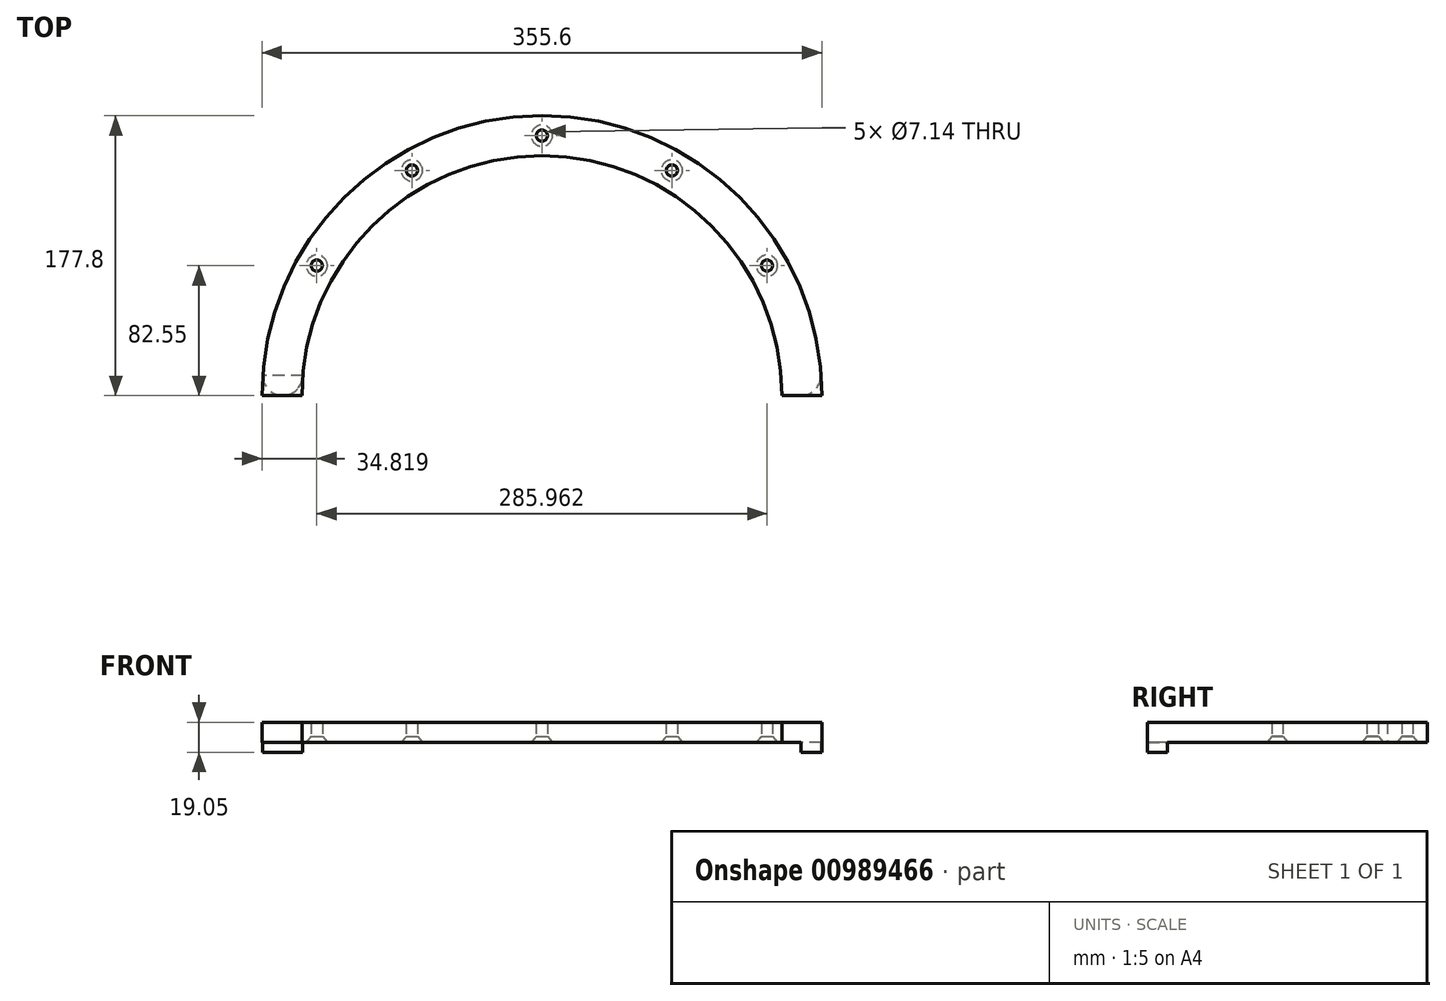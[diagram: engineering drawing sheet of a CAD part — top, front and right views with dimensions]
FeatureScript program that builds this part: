
annotation { "Feature Type Name" : "Feature", "Feature Type Description" : "" }
export const myFeature = defineFeature(function(context is Context, id is Id, definition is map)
    precondition{}
    {
        {
            var Q0;
            Q0=qCreatedBy(makeId("Top.planeOp"),FACE);
            var sketch = newSketch(context, id + "F0", { "sketchPlane" : qUnion([Q0])});
            skArc(sketch, "E0", {"start": v(-152.4, 0) * mm, "mid": v(0, 152.4) * mm, "end": v(152.4, 0) * mm});
            skArc(sketch, "E1", {"start": v(177.8, 0) * mm, "mid": v(0, 177.8) * mm, "end": v(-177.8, 0) * mm});
            skLineSegment(sketch, "E2", {"start": v(-177.8, 0) * mm, "end": v(-152.4, 0) * mm});
            skLineSegment(sketch, "E3", {"start": v(152.4, 0) * mm, "end": v(177.8, 0) * mm});
            skSolve(sketch);
        }
        {
            var Q0;
            Q0 = qSketchRegion(id + "F0", true);
            extrude(context, id + "F1", {"entities" : qUnion([Q0]), "depth" : 12.7 * mm, "offsetDistance" : 25.4 * mm});
        }
        {
            var Q0;
            Q0=makeQuery(id+"F1.opExtrude","CAP_FACE",FACE,{"disambiguationData":[OSD([sQuery(id+"F0.wireOp",EDGE,"E0"),sQuery(id+"F0.wireOp",EDGE,"E1"),sQuery(id+"F0.wireOp",EDGE,"E2"),sQuery(id+"F0.wireOp",EDGE,"E3")])],"isStart":true});
            var sketch = newSketch(context, id + "F2", { "sketchPlane" : qUnion([Q0])});
            skArc(sketch, "E4", {"start": v(-151.91, -12.7) * mm, "mid": v(-164.61, 0) * mm, "end": v(-177.31, -12.7) * mm});
            skLineSegment(sketch, "E5", {"start": v(-164.61, -12.7) * mm, "end": v(-151.87, -12.7) * mm});
            skLineSegment(sketch, "E6", {"start": v(-151.87, -12.7) * mm, "end": v(-177.35, -12.7) * mm});
            skLineSegment(sketch, "E7", {"start": v(0, 0) * mm, "end": v(0, -152.4) * mm});
            skArc(sketch, "E8.MirrorCS", {"start": v(151.91, -12.7) * mm, "mid": v(164.61, 0) * mm, "end": v(177.31, -12.7) * mm});
            skLineSegment(sketch, "E9.MirrorCS", {"start": v(151.87, -12.7) * mm, "end": v(177.35, -12.7) * mm});
            skSolve(sketch);
        }
        {
            var Q0;
            {var subQ0=sQuery(id+"F2.wireOp",EDGE,"E5");var subQ1=sQuery(id+"F2.wireOp",EDGE,"E4");var subQ2=makeQuery(id+"F2.imprint","INTERSECT",VERTEX,{"derivedFrom":[subQ1,subQ0]});Q0=makeQuery(id+"F2.imprint","IMPRINT",FACE,{"disambiguationData":[TD([[makeQuery(id+"F2.imprint","IMPRINT",EDGE,{"disambiguationData":[TD([[subQ2,-1.0]])],"derivedFrom":subQ1}),1.0]])]});}
            var Q1;
            {var subQ0=sQuery(id+"F2.wireOp",EDGE,"E9.MirrorCS");var subQ1=sQuery(id+"F2.wireOp",EDGE,"E8.MirrorCS");var subQ2=makeQuery(id+"F2.imprint","INTERSECT",VERTEX,{"disambiguationData":[OD(0.0)],"derivedFrom":[subQ1,subQ0]});Q1=makeQuery(id+"F2.imprint","IMPRINT",FACE,{"disambiguationData":[TD([[makeQuery(id+"F2.imprint","IMPRINT",EDGE,{"disambiguationData":[TD([[subQ2,-1.0]])],"derivedFrom":subQ1}),-1.0]])]});}
            extrude(context, id + "F3", {"entities" : qUnion([Q0, Q1]), "operationType" : NewBodyOperationType.ADD, "depth" : 6.35 * mm, "offsetDistance" : 25.4 * mm});
        }
        {
            var Q0;
            Q0=qCreatedBy(makeId("Top.planeOp"),FACE);
            var sketch = newSketch(context, id + "F4", { "sketchPlane" : qUnion([Q0])});
            skArc(sketch, "E10", {"start": v(-165.1, 0) * mm, "mid": v(0, 165.1) * mm, "end": v(165.1, 0) * mm});
            skPoint(sketch, "E11", {"position": v(-165.1, 0) * mm});
            skPoint(sketch, "E12.1.0", {"position": v(-142.98, 82.55) * mm});
            skPoint(sketch, "E12.2.0", {"position": v(-82.55, 142.98) * mm});
            skPoint(sketch, "E12.3.0", {"position": v(0, 165.1) * mm});
            skPoint(sketch, "E12.4.0", {"position": v(82.55, 142.98) * mm});
            skPoint(sketch, "E12.5.0", {"position": v(142.98, 82.55) * mm});
            skPoint(sketch, "E12.6.0", {"position": v(165.1, 0) * mm});
            skLineSegment(sketch, "E12.anchor1", {"start": v(0, 0) * mm, "end": v(-165.1, 0) * mm, "construction": true});
            skLineSegment(sketch, "E12.anchor2", {"start": v(0, 0) * mm, "end": v(165.1, 0) * mm, "construction": true});
            skSolve(sketch);
        }
        {
            var Q0;
            Q0=sQuery(id+"F4.wireOp",VERTEX,"E12.1.0");
            var Q1;
            Q1=sQuery(id+"F4.wireOp",VERTEX,"E12.2.0");
            var Q2;
            Q2=sQuery(id+"F4.wireOp",VERTEX,"E12.3.0");
            var Q3;
            Q3=sQuery(id+"F4.wireOp",VERTEX,"E12.4.0");
            var Q4;
            Q4=sQuery(id+"F4.wireOp",VERTEX,"E12.5.0");
            var Q5;
            Q5=makeQuery(id+"F1.opExtrude","SWEPT_BODY",BODY,{"disambiguationData":[OSD([sQuery(id+"F0.wireOp",EDGE,"E0"),sQuery(id+"F0.wireOp",EDGE,"E1"),sQuery(id+"F0.wireOp",EDGE,"E2"),sQuery(id+"F0.wireOp",EDGE,"E3")])]});
            hole(context, id + "F5", {"style" : HoleStyle.C_SINK, "endStyle" : HoleEndStyle.THROUGH, "oppositeDirection" : true, "standardTappedOrClearance" : lookupTablePath({ "fit" : "Normal (ASME)", "standard" : "ANSI", "size" : "1/4", "type" : "Clearance" }), "standardBlindInLast" : lookupTablePath({ "fit" : "Normal", "standard" : "ANSI", "engagement" : "75%", "pitch" : "20 tpi", "size" : "1/4", "type" : "Clearance & tapped" }), "holeDiameter" : 7.14 * mm, "cSinkDiameter" : 13.5 * mm, "cSinkAngle" : 82 * degree, "majorDiameter" : 6.35 * mm, "isTappedThrough" : true, "tappedDepth" : 12.7 * mm, "tapClearance" : 3, "locations" : qUnion([Q0, Q1, Q2, Q3, Q4]), "scope" : qUnion([Q5])});
        }
    });
